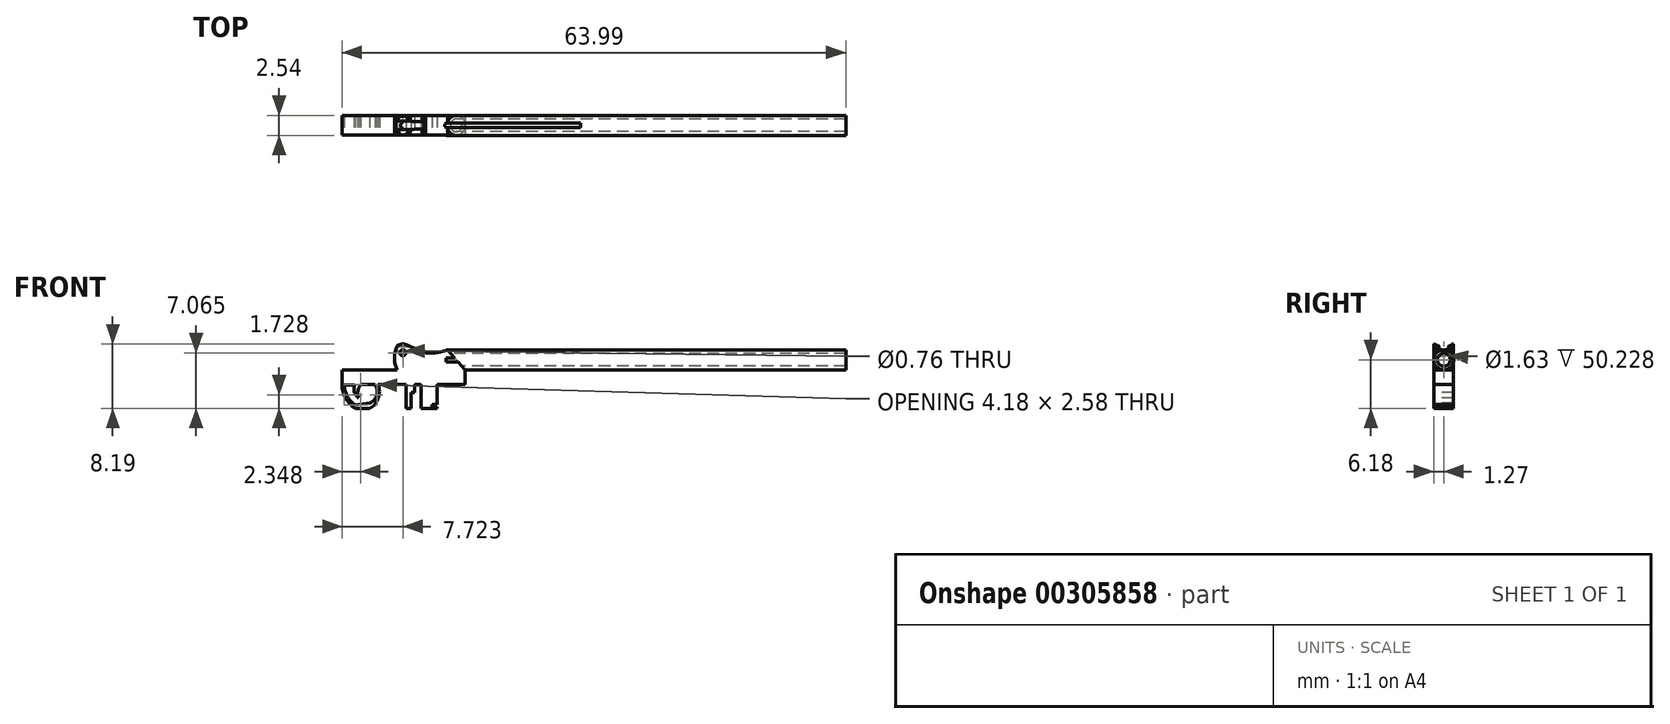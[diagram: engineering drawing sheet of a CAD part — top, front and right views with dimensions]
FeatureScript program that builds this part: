
annotation { "Feature Type Name" : "Feature", "Feature Type Description" : "" }
export const myFeature = defineFeature(function(context is Context, id is Id, definition is map)
    precondition{}
    {
        {
            var Q0;
            Q0=qCreatedBy(makeId("Front.planeOp"),FACE);
            var sketch = newSketch(context, id + "F0", { "sketchPlane" : qUnion([Q0])});
            skLineSegment(sketch, "E0", {"start": v(-17.1, 1.27) * mm, "end": v(33.7, 1.27) * mm});
            skLineSegment(sketch, "E1", {"start": v(33.7, 1.27) * mm, "end": v(33.7, 0) * mm});
            skLineSegment(sketch, "E2", {"start": v(33.7, 0) * mm, "end": v(-17.1, 0) * mm});
            skLineSegment(sketch, "E3", {"start": v(-17.1, 0) * mm, "end": v(-17.1, 1.27) * mm});
            skSolve(sketch);
        }
        {
            var Q0;
            Q0 = qSketchRegion(id + "F0", true);
            var Q1;
            Q1=sQuery(id+"F0.wireOp",EDGE,"E0");
            revolve(context, id + "F1", {"entities" : qUnion([Q0]), "axis" : qUnion([Q1]), "revolveType" : RevolveType.FULL});
        }
        {
            var Q0;
            Q0=makeQuery(id+"F1.opRevolve","SWEPT_FACE",FACE,{"disambiguationData":[OSD([sQuery(id+"F0.wireOp",EDGE,"E3")])]});
            var sketch = newSketch(context, id + "F2", { "sketchPlane" : qUnion([Q0])});
            skCircle(sketch, "E4", {"center": v(0, 1.27) * mm, "radius": 0.82 * mm});
            skSolve(sketch);
        }
        {
            var Q0;
            Q0=makeQuery(id+"F2.imprint","IMPRINT",FACE,{"disambiguationData":[TD([[makeQuery(id+"F2.imprint","IMPRINT",EDGE,{"derivedFrom":sQuery(id+"F2.wireOp",EDGE,"E4")}),1.0]])]});
            extrude(context, id + "F3", {"entities" : qUnion([Q0]), "operationType" : NewBodyOperationType.REMOVE, "endBound" : BoundingType.THROUGH_ALL, "oppositeDirection" : true, "depth" : 25.4 * mm});
        }
        {
            var Q0;
            Q0=qCreatedBy(makeId("Front.planeOp"),FACE);
            var sketch = newSketch(context, id + "F4", { "sketchPlane" : qUnion([Q0])});
            skLineSegment(sketch, "E5", {"start": v(-14.64, 0) * mm, "end": v(-14.64, -1.9) * mm});
            skLineSegment(sketch, "E6", {"start": v(-14.64, -1.9) * mm, "end": v(-18.21, -1.9) * mm});
            skLineSegment(sketch, "E7", {"start": v(-18.21, -1.9) * mm, "end": v(-18.21, -4.42) * mm});
            skLineSegment(sketch, "E8", {"start": v(-18.21, -4.42) * mm, "end": v(-18.83, -4.42) * mm});
            skLineSegment(sketch, "E9", {"start": v(-18.83, -4.42) * mm, "end": v(-18.83, -4.7) * mm});
            skLineSegment(sketch, "E10", {"start": v(-18.83, -4.7) * mm, "end": v(-18.21, -4.7) * mm});
            skLineSegment(sketch, "E11", {"start": v(-18.21, -4.7) * mm, "end": v(-18.21, -4.9) * mm});
            skLineSegment(sketch, "E12", {"start": v(-18.21, -4.9) * mm, "end": v(-20.28, -4.9) * mm});
            skLineSegment(sketch, "E13", {"start": v(-20.28, -4.9) * mm, "end": v(-20.28, -1.9) * mm});
            skLineSegment(sketch, "E14", {"start": v(-20.28, -1.9) * mm, "end": v(-21.06, -1.9) * mm});
            skLineSegment(sketch, "E15", {"start": v(-21.06, -1.9) * mm, "end": v(-21.06, -2.9) * mm});
            skLineSegment(sketch, "E16", {"start": v(-21.06, -2.9) * mm, "end": v(-21.5, -2.9) * mm});
            skLineSegment(sketch, "E17", {"start": v(-21.5, -2.9) * mm, "end": v(-21.5, -4.9) * mm});
            skLineSegment(sketch, "E18", {"start": v(-21.5, -4.9) * mm, "end": v(-22.19, -4.9) * mm});
            skLineSegment(sketch, "E19", {"start": v(-22.19, -4.9) * mm, "end": v(-22.19, -1.9) * mm});
            skLineSegment(sketch, "E20", {"start": v(-22.19, -1.9) * mm, "end": v(-27.06, -1.9) * mm});
            skLineSegment(sketch, "E21", {"start": v(-27.06, -1.9) * mm, "end": v(-25.58, 0) * mm});
            skLineSegment(sketch, "E22", {"start": v(-25.58, 0) * mm, "end": v(-23.3, 0) * mm});
            skArc(sketch, "E23", {"start": v(-23.3, 3) * mm, "mid": v(-23.64, 1.5) * mm, "end": v(-23.3, 0) * mm});
            skArc(sketch, "E24", {"start": v(-21.83, 3) * mm, "mid": v(-22.57, 3.28) * mm, "end": v(-23.3, 3) * mm});
            skArc(sketch, "E25", {"start": v(-21.68, 3) * mm, "mid": v(-20.94, 2.72) * mm, "end": v(-20.15, 2.76) * mm});
            skLineSegment(sketch, "E26", {"start": v(-21.68, 3) * mm, "end": v(-21.83, 3) * mm});
            skLineSegment(sketch, "E27", {"start": v(-20.15, 2.76) * mm, "end": v(-19.7, 2.15) * mm});
            skArc(sketch, "E28", {"start": v(-19.7, 2.15) * mm, "mid": v(-18.29, 2.18) * mm, "end": v(-16.93, 2.53) * mm});
            skLineSegment(sketch, "E29", {"start": v(-14.64, 0) * mm, "end": v(-16.93, 2.53) * mm});
            skLineSegment(sketch, "E30", {"start": v(-30.3, 0) * mm, "end": v(-25.58, 0) * mm});
            skPoint(sketch, "E30.startSnap0", {"position": v(-24.44, 0) * mm});
            skLineSegment(sketch, "E31", {"start": v(-30.3, 0) * mm, "end": v(-30.3, -1.9) * mm});
            skLineSegment(sketch, "E32", {"start": v(-30.3, -1.9) * mm, "end": v(-27.06, -1.9) * mm});
            skArc(sketch, "E33", {"start": v(-30.3, -1.9) * mm, "mid": v(-29.85, -3.62) * mm, "end": v(-28.63, -4.9) * mm});
            skArc(sketch, "E34", {"start": v(-26.79, -4.9) * mm, "mid": v(-25.69, -3.6) * mm, "end": v(-25.75, -1.9) * mm});
            skLineSegment(sketch, "E35", {"start": v(-26.79, -4.9) * mm, "end": v(-28.63, -4.9) * mm});
            skArc(sketch, "E36", {"start": v(-30.03, -1.9) * mm, "mid": v(-29.65, -3.36) * mm, "end": v(-28.63, -4.47) * mm});
            skArc(sketch, "E37", {"start": v(-26.79, -4.23) * mm, "mid": v(-25.91, -3.21) * mm, "end": v(-26.12, -1.9) * mm});
            skLineSegment(sketch, "E38", {"start": v(-26.79, -4.23) * mm, "end": v(-28.63, -4.47) * mm});
            skArc(sketch, "E39", {"start": v(-28.68, -1.9) * mm, "mid": v(-28.74, -2.82) * mm, "end": v(-28.2, -3.57) * mm});
            skArc(sketch, "E40", {"start": v(-27.94, -1.9) * mm, "mid": v(-28.3, -2.7) * mm, "end": v(-28.2, -3.57) * mm});
            skSolve(sketch);
        }
        {
            var Q0;
            Q0=makeQuery(id+"F4.imprint","IMPRINT",FACE,{"disambiguationData":[TD([[makeQuery(id+"F4.imprint","IMPRINT",EDGE,{"derivedFrom":sQuery(id+"F4.wireOp",EDGE,"E5")}),-1.0]])]});
            var Q1;
            Q1=makeQuery(id+"F4.imprint","IMPRINT",FACE,{"disambiguationData":[TD([[makeQuery(id+"F4.imprint","IMPRINT",EDGE,{"derivedFrom":sQuery(id+"F4.wireOp",EDGE,"E30")}),-1.0]])]});
            var Q2;
            {var subQ0=sQuery(id+"F4.wireOp",EDGE,"a4Uh2FE2-CU2P-4C1H-BZl5-eZaJ17gDqlyT");Q2=makeQuery(id+"F4.imprint","IMPRINT",FACE,{"disambiguationData":[TD([[makeQuery(id+"F4.imprint","IMPRINT",EDGE,{"derivedFrom":subQ0}),1.0]])]});}
            var Q3;
            {var subQ0=sQuery(id+"F4.wireOp",EDGE,"A0ScB6bT-KkhC-i5qG-928L-4w5cJB3wlSoS");Q3=makeQuery(id+"F4.imprint","IMPRINT",FACE,{"disambiguationData":[TD([[makeQuery(id+"F4.imprint","IMPRINT",EDGE,{"derivedFrom":subQ0}),1.0]])]});}
            var Q4;
            {var subQ1=sQuery(id+"F4.wireOp",EDGE,"E33");Q4=makeQuery(id+"F4.imprint","IMPRINT",FACE,{"disambiguationData":[TD([[makeQuery(id+"F4.imprint","IMPRINT",EDGE,{"derivedFrom":subQ1}),1.0]])]});}
            var Q5;
            {var subQ0=sQuery(id+"F4.wireOp",EDGE,"E39");Q5=makeQuery(id+"F4.imprint","IMPRINT",FACE,{"disambiguationData":[TD([[makeQuery(id+"F4.imprint","IMPRINT",EDGE,{"derivedFrom":subQ0}),1.0]])]});}
            extrude(context, id + "F5", {"entities" : qUnion([Q0, Q1, Q2, Q3, Q4, Q5]), "operationType" : NewBodyOperationType.ADD, "endBound" : BoundingType.SYMMETRIC, "oppositeDirection" : true, "depth" : 2.5 * mm});
        }
        {
            var Q0;
            Q0=makeQuery(id+"F5.opExtrude","CAP_FACE",FACE,{"disambiguationData":[OSD([sQuery(id+"F4.wireOp",EDGE,"E5"),sQuery(id+"F4.wireOp",EDGE,"E6"),sQuery(id+"F4.wireOp",EDGE,"E7"),sQuery(id+"F4.wireOp",EDGE,"E8"),sQuery(id+"F4.wireOp",EDGE,"E9"),sQuery(id+"F4.wireOp",EDGE,"E10"),sQuery(id+"F4.wireOp",EDGE,"E11"),sQuery(id+"F4.wireOp",EDGE,"E12"),sQuery(id+"F4.wireOp",EDGE,"E13"),sQuery(id+"F4.wireOp",EDGE,"E14"),sQuery(id+"F4.wireOp",EDGE,"E15"),sQuery(id+"F4.wireOp",EDGE,"E16"),sQuery(id+"F4.wireOp",EDGE,"E17"),sQuery(id+"F4.wireOp",EDGE,"E18"),sQuery(id+"F4.wireOp",EDGE,"E19"),sQuery(id+"F4.wireOp",EDGE,"E20"),sQuery(id+"F4.wireOp",EDGE,"E21"),sQuery(id+"F4.wireOp",EDGE,"E22"),sQuery(id+"F4.wireOp",EDGE,"E23"),sQuery(id+"F4.wireOp",EDGE,"E24"),sQuery(id+"F4.wireOp",EDGE,"E25"),sQuery(id+"F4.wireOp",EDGE,"E26"),sQuery(id+"F4.wireOp",EDGE,"E27"),sQuery(id+"F4.wireOp",EDGE,"E28"),sQuery(id+"F4.wireOp",EDGE,"E29")])],"isStart":false});
            var sketch = newSketch(context, id + "F6", { "sketchPlane" : qUnion([Q0])});
            skCircle(sketch, "E41", {"center": v(22.57, 2.15) * mm, "radius": 0.38 * mm});
            skSolve(sketch);
        }
        {
            var Q0;
            Q0=makeQuery(id+"F6.imprint","IMPRINT",FACE,{"disambiguationData":[TD([[makeQuery(id+"F6.imprint","IMPRINT",EDGE,{"derivedFrom":sQuery(id+"F6.wireOp",EDGE,"E41")}),1.0]])]});
            extrude(context, id + "F7", {"entities" : qUnion([Q0]), "operationType" : NewBodyOperationType.REMOVE, "endBound" : BoundingType.THROUGH_ALL, "oppositeDirection" : true, "depth" : 25.4 * mm});
        }
        {
            var Q0;
            Q0=qCreatedBy(makeId("Right.planeOp"),FACE);
            var sketch = newSketch(context, id + "F8", { "sketchPlane" : qUnion([Q0])});
            skArc(sketch, "E42", {"start": v(0.52, 2.95) * mm, "mid": v(0, 2.41) * mm, "end": v(-0.52, 2.94) * mm});
            skLineSegment(sketch, "E43", {"start": v(-0.52, 2.94) * mm, "end": v(-1.25, 3.29) * mm});
            skLineSegment(sketch, "E44", {"start": v(1.24, 3.28) * mm, "end": v(0.52, 2.95) * mm});
            skLineSegment(sketch, "E45", {"start": v(1.24, 3.28) * mm, "end": v(-1.25, 3.29) * mm});
            skSolve(sketch);
        }
        {
            var Q0;
            Q0 = qSketchRegion(id + "F8", true);
            extrude(context, id + "F9", {"entities" : qUnion([Q0]), "operationType" : NewBodyOperationType.REMOVE, "oppositeDirection" : true, "depth" : 25.65 * mm});
        }
    });
